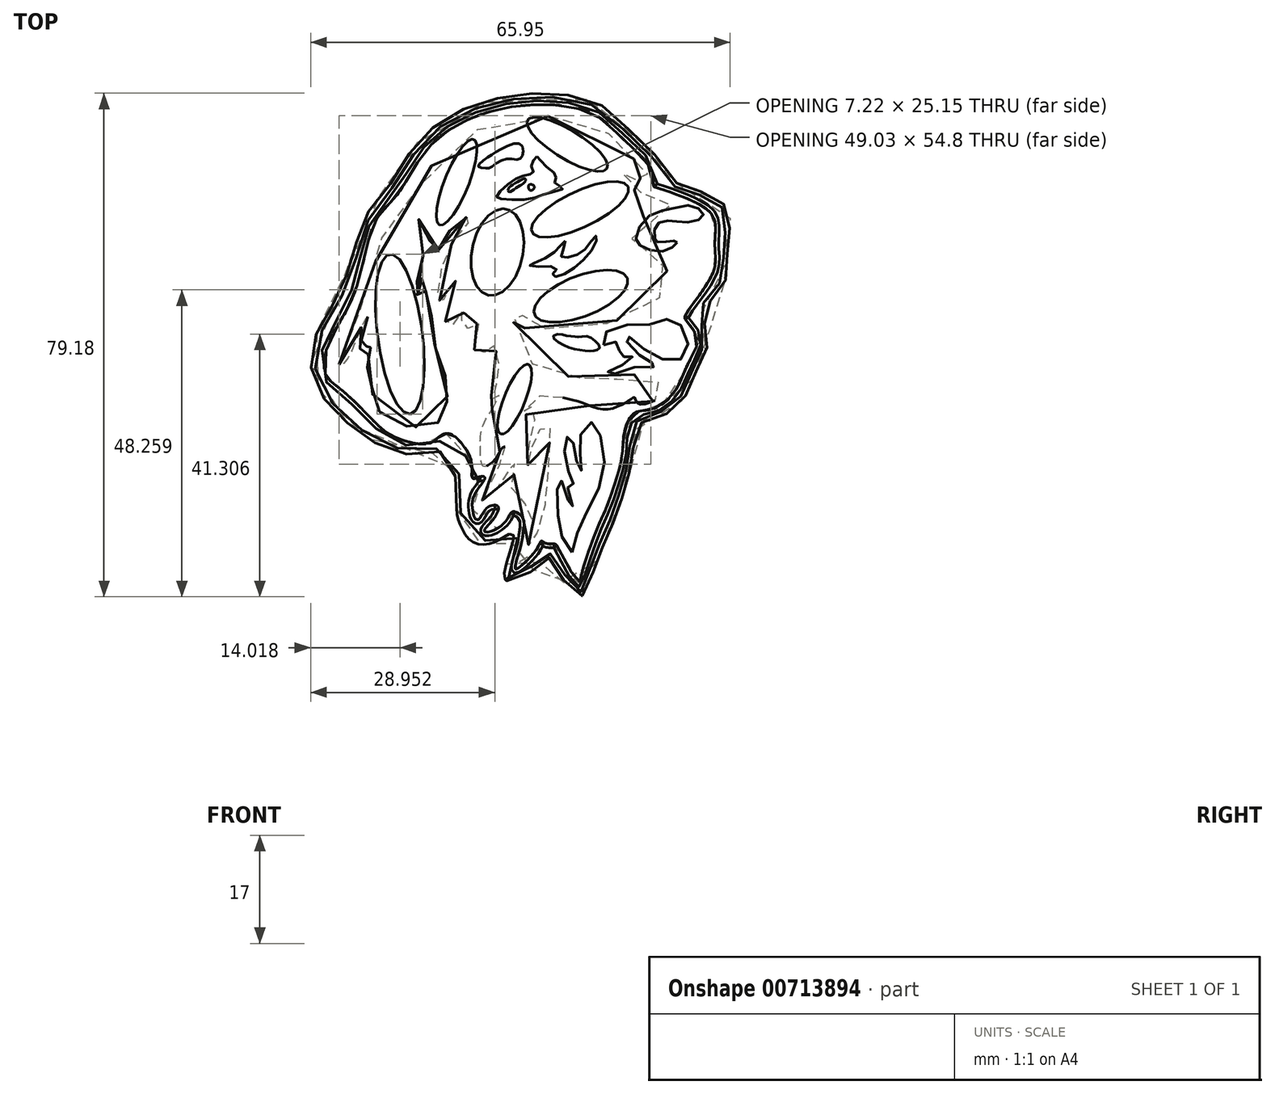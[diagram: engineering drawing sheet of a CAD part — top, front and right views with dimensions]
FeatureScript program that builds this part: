
annotation { "Feature Type Name" : "Feature", "Feature Type Description" : "" }
export const myFeature = defineFeature(function(context is Context, id is Id, definition is map)
    precondition{}
    {
        {
            var Q0;
            Q0=qCreatedBy(makeId("Top.planeOp"),FACE);
            var sketch = newSketch(context, id + "F0", { "sketchPlane" : qUnion([Q0])});
            skFitSpline(sketch, "E0", {"points": [v(-30.64, 5.6) * mm, v(-30.07, 10.5) * mm, v(-26, 18.48) * mm, v(-22.84, 29.5) * mm, v(-19.34, 33.79) * mm, v(-14.18, 41.45) * mm, v(-2.44, 47.38) * mm, v(11.25, 46.6) * mm, v(16.27, 42.4) * mm, v(20.43, 37.88) * mm, v(21, 35.04) * mm, v(21.14, 34.96) * mm, v(27.77, 32.46) * mm, v(30.58, 29.71) * mm, v(30.59, 25.88) * mm, v(30.29, 21.49) * mm, v(25.96, 14.86) * mm, v(26.07, 13.98) * mm, v(27.65, 11.77) * mm, v(27.58, 9.53) * mm, v(26.13, 6.7) * mm, v(24.09, 2.5) * mm, v(20.5, 0) * mm, v(17.97, -0.55) * mm, v(16.38, -3.47) * mm, v(16.02, -7.18) * mm, v(15.32, -10.21) * mm, v(13.63, -15.2) * mm, v(11.95, -19.1) * mm, v(9.44, -26.6) * mm, v(9.3, -27.28) * mm, v(8.75, -26.81) * mm, v(5.78, -21.4) * mm, v(5.33, -21.13) * mm, v(4.45, -21.11) * mm, v(3.78, -20.91) * mm, v(3.3, -20.66) * mm, v(2.75, -21.7) * mm, v(-0.6, -25.08) * mm, v(-0.82, -24.94) * mm, v(0.13, -21.27) * mm, v(0.5, -18.88) * mm, v(0.43, -17.11) * mm, v(-1.14, -16.05) * mm, v(-2.3, -17.59) * mm, v(-4.97, -19.24) * mm, v(-5.66, -19.06) * mm, v(-4.16, -17.17) * mm, v(-3.43, -15.37) * mm, v(-3.74, -15.06) * mm, v(-4.75, -15.18) * mm, v(-5.79, -16.1) * mm, v(-6.64, -17.36) * mm, v(-7.21, -17) * mm, v(-7.44, -16.06) * mm, v(-7.57, -15.16) * mm, v(-6.98, -12.98) * mm, v(-5.55, -10.77) * mm, v(-6, -10.5) * mm, v(-7.3, -10.87) * mm, v(-7.62, -10.43) * mm, v(-7.74, -7.93) * mm, v(-11.06, -3.82) * mm, v(-12.9, -4.4) * mm, v(-14.46, -5.4) * mm, v(-19.8, -4.3) * mm, v(-23, -1.84) * mm, v(-28.12, 3.1) * mm, v(-30.64, 5.6) * mm]});
            skFitSpline(sketch, "E1", {"points": [v(-0.16, 41.82) * mm, v(-3.52, 40.66) * mm, v(-5.31, 39.48) * mm, v(-6.6, 38.23) * mm, v(-5.52, 37.93) * mm, v(-4.6, 38.12) * mm, v(-2.34, 39.4) * mm, v(-0.25, 39.32) * mm, v(0.47, 40.3) * mm, v(-0.16, 41.82) * mm]});
            skFitSpline(sketch, "E2", {"points": [v(0.73, 36.33) * mm, v(0, 36.05) * mm, v(-1.48, 35.15) * mm, v(-1.94, 34.5) * mm, v(-1.7, 34.22) * mm, v(-0.64, 34.84) * mm, v(0.35, 35.45) * mm, v(0.88, 36.06) * mm, v(0.73, 36.33) * mm]});
            skFitSpline(sketch, "E3", {"points": [v(1.45, 35.36) * mm, v(1.3, 34.78) * mm, v(1.62, 34.43) * mm, v(2.03, 34.6) * mm, v(2.23, 34.92) * mm, v(2.1, 35.26) * mm, v(1.45, 35.36) * mm]});
            skFitSpline(sketch, "E4", {"points": [v(2.66, 39.8) * mm, v(3.05, 39.35) * mm, v(4.48, 37.9) * mm, v(5.62, 36.84) * mm, v(5.45, 36.13) * mm, v(5.52, 35.44) * mm, v(6.51, 35.01) * mm, v(6.65, 34.68) * mm, v(4.39, 34.06) * mm, v(2.07, 33.24) * mm, v(-1.52, 32.98) * mm, v(-3.58, 33.28) * mm, v(-3.69, 33.53) * mm, v(-2.61, 34.84) * mm, v(-0.55, 36.34) * mm, v(0.94, 36.86) * mm, v(1.9, 37.09) * mm, v(2.07, 37.43) * mm, v(1.73, 38.3) * mm, v(2.09, 39.21) * mm, v(2.66, 39.8) * mm]});
            skFitSpline(sketch, "E5", {"points": [v(-28.5, 7.07) * mm, v(-28.65, 8.26) * mm, v(-26.72, 13.04) * mm, v(-23.78, 18.54) * mm, v(-22.3, 25.34) * mm, v(-20.38, 29.15) * mm, v(-17.13, 32.83) * mm, v(-13.81, 38.47) * mm, v(-7.7, 43.48) * mm, v(-0.86, 45.96) * mm, v(5.38, 45.98) * mm, v(9.52, 45.08) * mm, v(13.07, 44.05) * mm, v(16.16, 40.89) * mm, v(18.94, 38.46) * mm, v(20.27, 36.38) * mm, v(20.37, 35.24) * mm, v(19.22, 35.4) * mm, v(17.96, 35.68) * mm, v(17.89, 36.15) * mm, v(18.83, 36.08) * mm, v(18.17, 37.73) * mm, v(17.65, 37.98) * mm, v(16.92, 36.7) * mm, v(15.48, 37.6) * mm, v(15.36, 37.21) * mm, v(16.54, 35.8) * mm, v(18, 34.5) * mm, v(21.96, 33.75) * mm, v(24.66, 33) * mm, v(24.57, 32.4) * mm, v(21.9, 31.93) * mm, v(18.68, 29.77) * mm, v(17.56, 26.9) * mm, v(18.92, 24.73) * mm, v(20.55, 23.57) * mm, v(22.01, 23.05) * mm, v(23.4, 21.42) * mm, v(24.54, 20.44) * mm, v(22.72, 18) * mm, v(20.31, 16.92) * mm, v(16.23, 14.4) * mm, v(12.96, 13.3) * mm, v(11.07, 12.5) * mm, v(4.38, 12.64) * mm, v(1.43, 12.75) * mm, v(0.31, 12.92) * mm, v(0, 13.36) * mm, v(0.32, 14.57) * mm, v(0.45, 15.51) * mm, v(0.53, 16.63) * mm, v(0.27, 16.95) * mm, v(-0.48, 15.28) * mm, v(-1.09, 13.55) * mm, v(-0.87, 10.95) * mm, v(0.96, 8.03) * mm, v(4.11, 5.9) * mm, v(6.8, 5.37) * mm, v(9.42, 4.98) * mm, v(10.87, 5.32) * mm, v(12.56, 3.91) * mm, v(14.57, 4.32) * mm, v(16.68, 5.63) * mm, v(19.25, 4.86) * mm, v(20.87, 4.12) * mm, v(23.07, 4.7) * mm, v(23.88, 4.58) * mm, v(22.86, 3.06) * mm, v(20.95, 1.34) * mm, v(18.42, 1) * mm, v(17.98, 1.9) * mm, v(17.43, 1.65) * mm, v(16.09, 0.84) * mm, v(13.31, 0) * mm, v(9.98, 0.97) * mm, v(6.76, 1.84) * mm, v(3.87, 2.25) * mm, v(1.5, 1.26) * mm, v(0.6, -0.63) * mm, v(1.01, -0.75) * mm, v(1.7, 0.44) * mm, v(2.2, 0.36) * mm, v(2.27, -1.57) * mm, v(1.47, -4.97) * mm, v(1.05, -7.68) * mm, v(1.27, -8.87) * mm, v(1.69, -6.57) * mm, v(2.45, -4.42) * mm, v(3.5, -2.66) * mm, v(4.38, -2.22) * mm, v(4.67, -4.14) * mm, v(4.08, -13.12) * mm, v(3.13, -18.28) * mm, v(1.74, -21.07) * mm, v(1.41, -21.4) * mm, v(1.3, -20.79) * mm, v(2.07, -17.34) * mm, v(1.55, -15.3) * mm, v(-1.13, -13.62) * mm, v(-1.13, -11.22) * mm, v(-0.92, -8.3) * mm, v(-1.12, -7.88) * mm, v(-1.36, -8.38) * mm, v(-2.84, -11.86) * mm, v(-4.47, -13.05) * mm, v(-5.6, -14.29) * mm, v(-6.22, -13.96) * mm, v(-4.91, -12.03) * mm, v(-3.44, -9.39) * mm, v(-2.76, -7.07) * mm, v(-2.43, -5.86) * mm, v(-2.91, -6.15) * mm, v(-4.01, -7.9) * mm, v(-5.77, -8.93) * mm, v(-6.24, -7.1) * mm, v(-6.07, -3.14) * mm, v(-4.4, 0) * mm], "startDerivative": vector(-134.43, 141.78) * mm, "endDerivative": vector(189.44, 268.7) * mm});
            skFitSpline(sketch, "E6", {"points": [v(-4.4, 0) * mm, v(-3.25, 2.1) * mm, v(-3.58, 2.23) * mm, v(-4.02, 1.62) * mm, v(-4.52, 2.02) * mm, v(-3.5, 4.44) * mm, v(-3.5, 7.97) * mm, v(-4.3, 10.14) * mm, v(-5.27, 9.32) * mm, v(-6.61, 8.7) * mm, v(-7.38, 10.42) * mm, v(-6.56, 12.22) * mm, v(-6.24, 13.17) * mm, v(-6.72, 13.5) * mm, v(-7.9, 12.84) * mm, v(-9.12, 13.04) * mm, v(-9.04, 14.47) * mm, v(-8.95, 15.4) * mm, v(-9.64, 14.9) * mm, v(-10.87, 13.12) * mm, v(-11.68, 13.52) * mm, v(-11.35, 15.98) * mm, v(-10.42, 19.18) * mm, v(-10.22, 20.25) * mm, v(-10.85, 19.5) * mm, v(-11.67, 17.7) * mm, v(-12.49, 17.05) * mm, v(-12.9, 17.95) * mm, v(-11.86, 23.73) * mm, v(-8.72, 28.77) * mm, v(-7.78, 29.84) * mm, v(-8.07, 30.25) * mm, v(-9.5, 29.63) * mm, v(-12.14, 26.72) * mm, v(-13, 24.91) * mm, v(-13.49, 24.87) * mm, v(-14.94, 28.56) * mm, v(-16.08, 29.9) * mm, v(-16.12, 29.16) * mm, v(-15.6, 27.65) * mm, v(-15.4, 23.23) * mm, v(-16.38, 19.4) * mm, v(-16.32, 17.98) * mm, v(-15.98, 18.52) * mm, v(-15.7, 20.28) * mm, v(-15.17, 20.6) * mm, v(-14.8, 18.2) * mm, v(-14.07, 15.25) * mm, v(-13.23, 9.27) * mm, v(-11.57, 4.56) * mm, v(-11.65, 0.57) * mm, v(-12.96, -2.1) * mm, v(-19.13, -2.3) * mm, v(-22.87, 0.92) * mm, v(-23.46, 4.57) * mm, v(-24.04, 6.7) * mm, v(-23.79, 9.1) * mm, v(-23.43, 10.47) * mm, v(-23.93, 10.31) * mm, v(-24.42, 9.63) * mm, v(-25.17, 9.56) * mm, v(-23.87, 14.12) * mm, v(-24.02, 14.56) * mm, v(-25.97, 10.5) * mm, v(-27.14, 8.06) * mm, v(-28.5, 7.07) * mm], "startDerivative": vector(112.78, 154.63) * mm, "endDerivative": vector(-106.75, 41.5) * mm});
            skFitSpline(sketch, "E7", {"points": [v(24.68, 26.24) * mm, v(24.06, 25.63) * mm, v(21.89, 24.84) * mm, v(19, 25.72) * mm, v(18.2, 26.71) * mm, v(19.82, 30.12) * mm, v(23.62, 31.54) * mm, v(26.92, 32.07) * mm, v(28.7, 31) * mm, v(28.7, 30.33) * mm, v(26.78, 29.46) * mm, v(24.29, 29.6) * mm, v(22.7, 29.62) * mm, v(21.26, 28.87) * mm, v(21.13, 27.08) * mm, v(21.29, 26.38) * mm, v(22.2, 26.33) * mm, v(23.7, 26.44) * mm, v(24.51, 26.54) * mm, v(24.68, 26.24) * mm]});
            skFitSpline(sketch, "E8", {"points": [v(7.05, 26.5) * mm, v(6.84, 25.4) * mm, v(6.52, 23.94) * mm, v(7.95, 24.02) * mm, v(9.83, 24.86) * mm, v(11.17, 26.5) * mm, v(11.9, 27.29) * mm, v(12.05, 27) * mm, v(11.25, 25.02) * mm, v(8.9, 22.63) * mm, v(6.47, 21.11) * mm, v(5.24, 20.94) * mm, v(5.12, 21.3) * mm, v(5.67, 21.88) * mm, v(5.42, 22.37) * mm, v(2.84, 22.44) * mm, v(1.45, 22.7) * mm, v(2.44, 23.12) * mm, v(5.09, 24.5) * mm, v(6.37, 25.84) * mm, v(7.05, 26.5) * mm]});
            skFitSpline(sketch, "E9", {"points": [v(12.09, 9.36) * mm, v(12.5, 9.8) * mm, v(11.73, 10.75) * mm, v(10.47, 11.55) * mm, v(9.18, 11.4) * mm, v(8.52, 11.5) * mm, v(7.34, 11.56) * mm, v(6.18, 11.83) * mm, v(5.18, 11.51) * mm, v(6.1, 10.5) * mm, v(8.05, 9.64) * mm, v(10, 9.25) * mm, v(11.35, 9.2) * mm, v(12.09, 9.36) * mm]});
            skFitSpline(sketch, "E10", {"points": [v(13.12, 10.12) * mm, v(13.07, 11.4) * mm, v(14.08, 12.63) * mm, v(17.94, 13.4) * mm, v(20.94, 13.42) * mm, v(22.9, 14.18) * mm, v(24.1, 14.3) * mm, v(26.16, 11.76) * mm, v(26.3, 9.73) * mm, v(25.32, 7.94) * mm, v(23.21, 7.67) * mm, v(20.57, 8.75) * mm, v(18.14, 10.62) * mm, v(16.8, 11.56) * mm, v(16.25, 11.4) * mm, v(17.66, 9.8) * mm, v(18.8, 8.5) * mm, v(19.34, 7.67) * mm, v(21.6, 7.1) * mm, v(21.55, 6.69) * mm, v(19.82, 6.93) * mm, v(17.13, 6.41) * mm, v(14.7, 5.55) * mm, v(13.89, 5.35) * mm, v(13.75, 5.82) * mm, v(14.77, 6.55) * mm, v(16.77, 7.3) * mm, v(17.6, 8) * mm, v(17.52, 8.51) * mm, v(17.02, 8.59) * mm, v(16.17, 8.3) * mm, v(15.43, 8.45) * mm, v(15.58, 9.18) * mm, v(15.6, 10.4) * mm, v(15.15, 10.65) * mm, v(14, 10.2) * mm, v(13.12, 10.12) * mm]});
            skFitSpline(sketch, "E11", {"points": [v(8.15, -22.42) * mm, v(6.86, -20.67) * mm, v(6.02, -17.62) * mm, v(5.78, -12.82) * mm, v(6.18, -10.83) * mm, v(6.96, -12.46) * mm, v(7.76, -14.94) * mm, v(8.2, -15.48) * mm, v(8.07, -14.47) * mm, v(7.41, -11.83) * mm, v(7.72, -11.22) * mm, v(8.45, -11.67) * mm, v(8.33, -11.12) * mm, v(7, -8.2) * mm, v(7.05, -5.7) * mm, v(7.3, -4.45) * mm, v(7.8, -4.02) * mm, v(8.36, -5.2) * mm, v(8.77, -7.82) * mm, v(9.2, -8.88) * mm, v(9.57, -9.62) * mm, v(9.59, -8.36) * mm, v(9.32, -6.01) * mm, v(9.74, -3.28) * mm, v(11.18, -2) * mm, v(12.03, -2.73) * mm, v(13.2, -6.9) * mm, v(12.54, -11.9) * mm, v(10.13, -16.74) * mm, v(8.9, -19.73) * mm, v(8.15, -22.42) * mm]});
            skLineSegment(sketch, "E12.bottom", {"start": v(78.6, 32.61) * mm, "end": v(148.5, 32.61) * mm});
            skLineSegment(sketch, "E12.top", {"start": v(78.6, -48.55) * mm, "end": v(148.5, -48.55) * mm});
            skLineSegment(sketch, "E12.left", {"start": v(78.6, 32.61) * mm, "end": v(78.6, -48.55) * mm});
            skLineSegment(sketch, "E12.right", {"start": v(148.5, 32.61) * mm, "end": v(148.5, -48.55) * mm});
            skLineSegment(sketch, "E13.bottom", {"start": v(-37.55, 55.64) * mm, "end": v(38.05, 55.64) * mm});
            skLineSegment(sketch, "E13.top", {"start": v(-37.55, -31.67) * mm, "end": v(38.05, -31.67) * mm});
            skLineSegment(sketch, "E13.left", {"start": v(-37.55, 55.64) * mm, "end": v(-37.55, -31.67) * mm});
            skLineSegment(sketch, "E13.right", {"start": v(38.05, 55.64) * mm, "end": v(38.05, -31.67) * mm});
            skPoint(sketch, "E14", {"position": v(-71.08, 31.25) * mm});
            skFitSpline(sketch, "E15", {"points": [v(-10, -15.59) * mm, v(-9.49, -12.73) * mm, v(-10.07, -11.41) * mm, v(-10.43, -8.48) * mm, v(-11.74, -6.58) * mm, v(-13.9, -7) * mm, v(-21.12, -6.07) * mm, v(-29.38, 0) * mm, v(-32.65, 5.35) * mm, v(-32.19, 11.64) * mm, v(-27.9, 19.53) * mm, v(-24.3, 30.35) * mm, v(-20.7, 35.05) * mm, v(-15.35, 42.85) * mm, v(-2.76, 49.11) * mm, v(11.96, 48.23) * mm, v(17.85, 43.23) * mm, v(22.25, 38.78) * mm, v(23.53, 36.33) * mm, v(26.06, 35.06) * mm, v(32.57, 31.6) * mm, v(32.51, 25.62) * mm, v(32.07, 19.92) * mm, v(28.37, 14.72) * mm, v(29.7, 12.58) * mm, v(29.1, 9.23) * mm, v(27.59, 5.93) * mm, v(24.17, 0) * mm, v(18.77, -2.28) * mm, v(17.68, -7) * mm, v(14.55, -17.88) * mm, v(11.73, -24.68) * mm, v(9.32, -29.45) * mm, v(5.52, -24.67) * mm, v(4, -23.02) * mm, v(2.43, -24.85) * mm, v(-2.34, -26.75) * mm, v(-1.03, -19.95) * mm, v(-1.6, -19.53) * mm, v(-3.9, -20.84) * mm, v(-7.36, -20.9) * mm, v(-9.08, -18.86) * mm, v(-10, -15.59) * mm]});
            skEllipse(sketch, "E16", {"center": v(-3.59, 24.74) * mm, "majorRadius": 6.93 * mm, "minorRadius": 4.01 * mm, "majorAxis": v(-0.2, -0.98)});
            skEllipse(sketch, "E17", {"center": v(9.53, 17.82) * mm, "majorRadius": 7.85 * mm, "minorRadius": 3.2 * mm, "majorAxis": v(0.93, 0.37)});
            skEllipse(sketch, "E18", {"center": v(9.39, 31.47) * mm, "majorRadius": 8.38 * mm, "minorRadius": 2.84 * mm, "majorAxis": v(0.9, 0.43)});
            skEllipse(sketch, "E19", {"center": v(7.4, 41.68) * mm, "majorRadius": 7.32 * mm, "minorRadius": 2.25 * mm, "majorAxis": v(0.85, -0.52)});
            skEllipse(sketch, "E20", {"center": v(-0.88, 1.62) * mm, "majorRadius": 5.9 * mm, "minorRadius": 1.67 * mm, "majorAxis": v(-0.37, -0.93)});
            skEllipse(sketch, "E21", {"center": v(-18.92, 11.86) * mm, "majorRadius": 12.68 * mm, "minorRadius": 3.54 * mm, "majorAxis": v(0.13, -1)});
            skEllipse(sketch, "E22", {"center": v(-10, 35.72) * mm, "majorRadius": 7.25 * mm, "minorRadius": 1.9 * mm, "majorAxis": v(-0.37, -0.93)});
            skSolve(sketch);
        }
        {
            var Q0;
            Q0=makeQuery(id+"F0.imprint","IMPRINT",FACE,{"disambiguationData":[TD([[makeQuery(id+"F0.imprint","IMPRINT",EDGE,{"derivedFrom":sQuery(id+"F0.wireOp",EDGE,"E0")}),-1.0]])]});
            var Q1;
            Q1=makeQuery(id+"F0.imprint","IMPRINT",FACE,{"disambiguationData":[TD([[makeQuery(id+"F0.imprint","IMPRINT",EDGE,{"derivedFrom":sQuery(id+"F0.wireOp",EDGE,"E8")}),-1.0]])]});
            var Q2;
            Q2=makeQuery(id+"F0.imprint","IMPRINT",FACE,{"disambiguationData":[TD([[makeQuery(id+"F0.imprint","IMPRINT",EDGE,{"derivedFrom":sQuery(id+"F0.wireOp",EDGE,"E2")}),-1.0]])]});
            var Q3;
            Q3=makeQuery(id+"F0.imprint","IMPRINT",FACE,{"disambiguationData":[TD([[makeQuery(id+"F0.imprint","IMPRINT",EDGE,{"derivedFrom":sQuery(id+"F0.wireOp",EDGE,"E1")}),1.0]])]});
            extrude(context, id + "F1", {"entities" : qUnion([Q0, Q1, Q2, Q3]), "depth" : 10 * mm, "offsetDistance" : 25 * mm});
        }
        {
            var Q0;
            Q0=makeQuery(id+"F0.imprint","IMPRINT",FACE,{"disambiguationData":[TD([[makeQuery(id+"F0.imprint","IMPRINT",EDGE,{"derivedFrom":sQuery(id+"F0.wireOp",EDGE,"E0")}),1.0]])]});
            var Q1;
            Q1=makeQuery(id+"F0.imprint","IMPRINT",FACE,{"disambiguationData":[TD([[makeQuery(id+"F0.imprint","IMPRINT",EDGE,{"derivedFrom":sQuery(id+"F0.wireOp",EDGE,"E1")}),-1.0]])]});
            var Q2;
            Q2=makeQuery(id+"F0.imprint","IMPRINT",FACE,{"disambiguationData":[TD([[makeQuery(id+"F0.imprint","IMPRINT",EDGE,{"derivedFrom":sQuery(id+"F0.wireOp",EDGE,"E0")}),-1.0]])]});
            var Q3;
            Q3=makeQuery(id+"F0.imprint","IMPRINT",FACE,{"disambiguationData":[TD([[makeQuery(id+"F0.imprint","IMPRINT",EDGE,{"derivedFrom":sQuery(id+"F0.wireOp",EDGE,"E7")}),-1.0]])]});
            var Q4;
            Q4=makeQuery(id+"F0.imprint","IMPRINT",FACE,{"disambiguationData":[TD([[makeQuery(id+"F0.imprint","IMPRINT",EDGE,{"derivedFrom":sQuery(id+"F0.wireOp",EDGE,"E2")}),-1.0]])]});
            var Q5;
            Q5=makeQuery(id+"F0.imprint","IMPRINT",FACE,{"disambiguationData":[TD([[makeQuery(id+"F0.imprint","IMPRINT",EDGE,{"derivedFrom":sQuery(id+"F0.wireOp",EDGE,"E1")}),1.0]])]});
            var Q6;
            Q6=makeQuery(id+"F0.imprint","IMPRINT",FACE,{"disambiguationData":[TD([[makeQuery(id+"F0.imprint","IMPRINT",EDGE,{"derivedFrom":sQuery(id+"F0.wireOp",EDGE,"E8")}),-1.0]])]});
            var Q7;
            Q7=makeQuery(id+"F0.imprint","IMPRINT",FACE,{"disambiguationData":[TD([[makeQuery(id+"F0.imprint","IMPRINT",EDGE,{"derivedFrom":sQuery(id+"F0.wireOp",EDGE,"E3")}),1.0]])]});
            var Q8;
            Q8=makeQuery(id+"F0.imprint","IMPRINT",FACE,{"disambiguationData":[TD([[makeQuery(id+"F0.imprint","IMPRINT",EDGE,{"derivedFrom":sQuery(id+"F0.wireOp",EDGE,"E2")}),1.0]])]});
            var Q9;
            Q9=makeQuery(id+"F0.imprint","IMPRINT",FACE,{"disambiguationData":[TD([[makeQuery(id+"F0.imprint","IMPRINT",EDGE,{"derivedFrom":sQuery(id+"F0.wireOp",EDGE,"E10")}),-1.0]])]});
            var Q10;
            Q10=makeQuery(id+"F0.imprint","IMPRINT",FACE,{"disambiguationData":[TD([[makeQuery(id+"F0.imprint","IMPRINT",EDGE,{"derivedFrom":sQuery(id+"F0.wireOp",EDGE,"E11")}),-1.0]])]});
            var Q11;
            Q11=makeQuery(id+"F0.imprint","IMPRINT",FACE,{"disambiguationData":[TD([[makeQuery(id+"F0.imprint","IMPRINT",EDGE,{"derivedFrom":sQuery(id+"F0.wireOp",EDGE,"E9")}),1.0]])]});
            extrude(context, id + "F2", {"entities" : qUnion([Q0, Q1, Q2, Q3, Q4, Q5, Q6, Q7, Q8, Q9, Q10, Q11]), "oppositeDirection" : true, "depth" : 2 * mm, "offsetDistance" : 25 * mm});
        }
        {
            var Q0;
            Q0=makeQuery(id+"F0.imprint","IMPRINT",FACE,{"disambiguationData":[TD([[makeQuery(id+"F0.imprint","IMPRINT",EDGE,{"derivedFrom":sQuery(id+"F0.wireOp",EDGE,"E0")}),1.0]])]});
            extrude(context, id + "F3", {"entities" : qUnion([Q0]), "depth" : 15 * mm, "offsetDistance" : 25 * mm});
        }
        {
            var Q0;
            Q0=makeQuery(id+"F0.imprint","IMPRINT",FACE,{"disambiguationData":[TD([[makeQuery(id+"F0.imprint","IMPRINT",EDGE,{"derivedFrom":sQuery(id+"F0.wireOp",EDGE,"E21")}),1.0]])]});
            var Q1;
            Q1=makeQuery(id+"F0.imprint","IMPRINT",FACE,{"disambiguationData":[TD([[makeQuery(id+"F0.imprint","IMPRINT",EDGE,{"derivedFrom":sQuery(id+"F0.wireOp",EDGE,"E22")}),1.0]])]});
            var Q2;
            Q2=makeQuery(id+"F0.imprint","IMPRINT",FACE,{"disambiguationData":[TD([[makeQuery(id+"F0.imprint","IMPRINT",EDGE,{"derivedFrom":sQuery(id+"F0.wireOp",EDGE,"E19")}),1.0]])]});
            var Q3;
            Q3=makeQuery(id+"F0.imprint","IMPRINT",FACE,{"disambiguationData":[TD([[makeQuery(id+"F0.imprint","IMPRINT",EDGE,{"derivedFrom":sQuery(id+"F0.wireOp",EDGE,"E16")}),1.0]])]});
            var Q4;
            Q4=makeQuery(id+"F0.imprint","IMPRINT",FACE,{"disambiguationData":[TD([[makeQuery(id+"F0.imprint","IMPRINT",EDGE,{"derivedFrom":sQuery(id+"F0.wireOp",EDGE,"E18")}),1.0]])]});
            var Q5;
            Q5=makeQuery(id+"F0.imprint","IMPRINT",FACE,{"disambiguationData":[TD([[makeQuery(id+"F0.imprint","IMPRINT",EDGE,{"derivedFrom":sQuery(id+"F0.wireOp",EDGE,"E17")}),1.0]])]});
            extrude(context, id + "F4", {"entities" : qUnion([Q0, Q1, Q2, Q3, Q4, Q5]), "operationType" : NewBodyOperationType.REMOVE, "oppositeDirection" : true, "depth" : 25 * mm, "offsetDistance" : 25 * mm});
        }
        {
            var Q0;
            Q0=makeQuery(id+"F3.opExtrude","CAP_FACE",FACE,{"disambiguationData":[OSD([sQuery(id+"F0.wireOp",EDGE,"E0"),sQuery(id+"F0.wireOp",EDGE,"E15")])],"isStart":false});
            fillet(context, id + "F5", {"entities" : qUnion([Q0]), "radius" : .6 * mm, "tangentPropagation" : true, "allowEdgeOverflow" : false});
        }
    });
